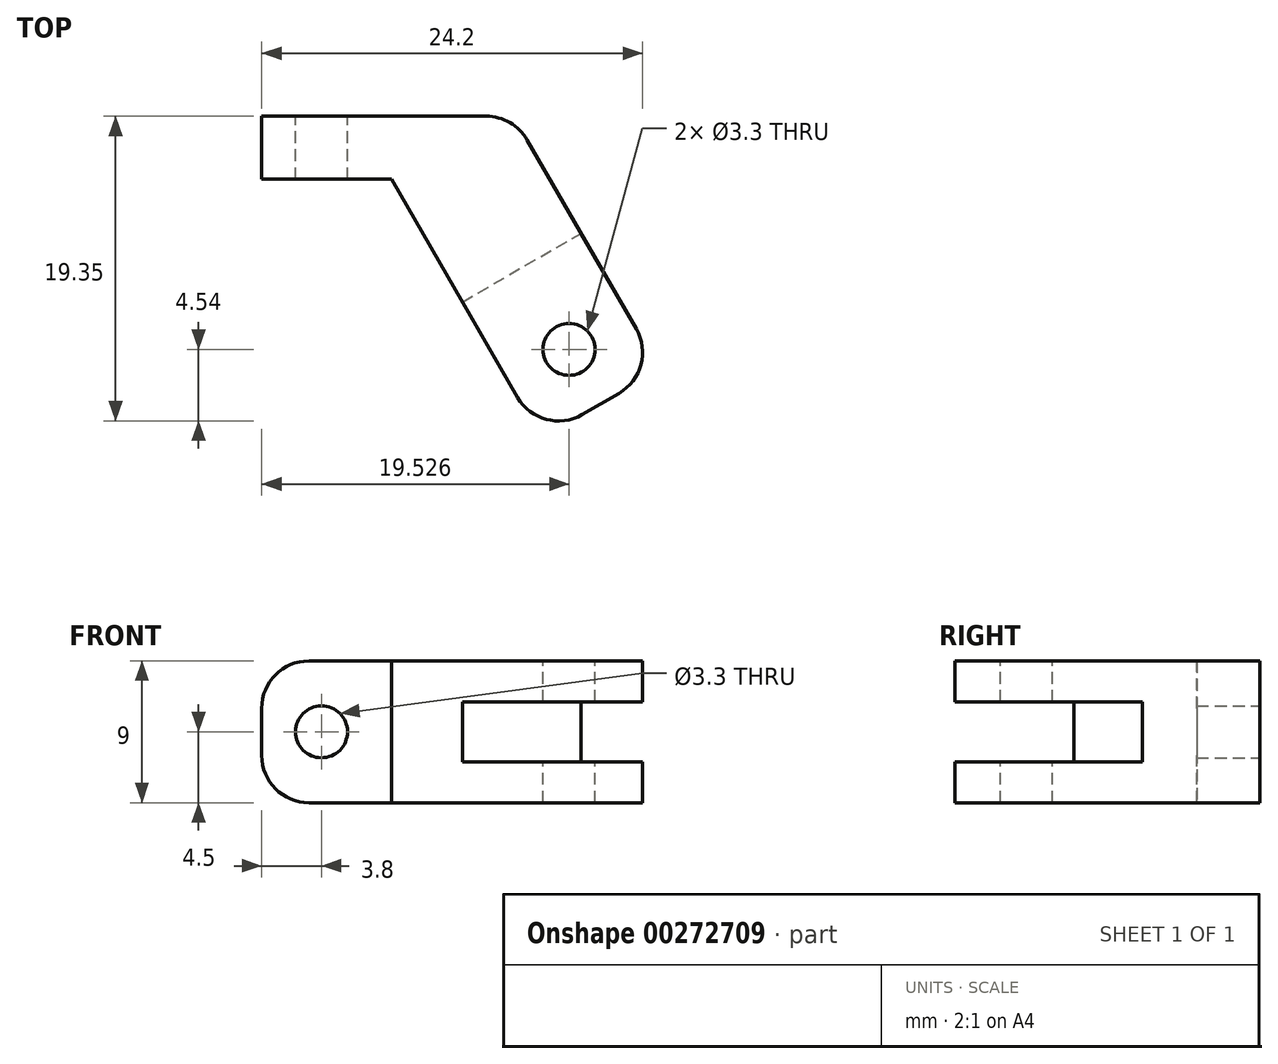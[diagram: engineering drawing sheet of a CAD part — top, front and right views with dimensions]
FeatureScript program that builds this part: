
annotation { "Feature Type Name" : "Feature", "Feature Type Description" : "" }
export const myFeature = defineFeature(function(context is Context, id is Id, definition is map)
    precondition{}
    {
        {
            var Q0;
            Q0=qCreatedBy(makeId("Top.planeOp"),FACE);
            var sketch = newSketch(context, id + "F0", { "sketchPlane" : qUnion([Q0])});
            skLineSegment(sketch, "E0.bottom", {"start": v(-8, 2) * mm, "end": v(8, 2) * mm});
            skLineSegment(sketch, "E0.top", {"start": v(-8, -2) * mm, "end": v(0.26, -2) * mm});
            skLineSegment(sketch, "E0.left", {"start": v(-8, 2) * mm, "end": v(-8, -2) * mm});
            skPoint(sketch, "E0.middle", {"position": v(0, 0) * mm});
            skLineSegment(sketch, "E1", {"start": v(8, 2) * mm, "end": v(17.3, -14.1) * mm});
            skLineSegment(sketch, "E2", {"start": v(17.3, -14.1) * mm, "end": v(9.76, -18.45) * mm});
            skLineSegment(sketch, "E3", {"start": v(9.76, -18.45) * mm, "end": v(0.26, -2) * mm});
            skPoint(sketch, "E4.orphan", {"position": v(8, -2) * mm});
            skSolve(sketch);
        }
        {
            var Q0;
            Q0 = qSketchRegion(id + "F0", true);
            extrude(context, id + "F1", {"entities" : qUnion([Q0]), "depth" : 9 * mm});
        }
        {
            var Q0;
            Q0=makeQuery(id+"F1.opExtrude","SWEPT_FACE",FACE,{"disambiguationData":[OSD([sQuery(id+"F0.wireOp",EDGE,"E0.bottom")])]});
            var sketch = newSketch(context, id + "F2", { "sketchPlane" : qUnion([Q0])});
            skLineSegment(sketch, "E5", {"start": v(8, 4.5) * mm, "end": v(-8, 4.5) * mm, "construction": true});
            skPoint(sketch, "E6", {"position": v(4.2, 4.5) * mm});
            skSolve(sketch);
        }
        {
            var Q0;
            Q0=makeQuery(id+"F1.opExtrude","SWEPT_FACE",FACE,{"disambiguationData":[OSD([sQuery(id+"F0.wireOp",EDGE,"E1")])]});
            var sketch = newSketch(context, id + "F3", { "sketchPlane" : qUnion([Q0])});
            skLineSegment(sketch, "E7", {"start": v(-20.86, 4.5) * mm, "end": v(-2.27, 4.5) * mm, "construction": true});
            skLineSegment(sketch, "E8.bottom", {"start": v(-10.86, 2.6) * mm, "end": v(-30.86, 2.6) * mm});
            skLineSegment(sketch, "E8.top", {"start": v(-10.86, 6.4) * mm, "end": v(-30.86, 6.4) * mm});
            skLineSegment(sketch, "E8.left", {"start": v(-10.86, 2.6) * mm, "end": v(-10.86, 6.4) * mm});
            skLineSegment(sketch, "E8.right", {"start": v(-30.86, 2.6) * mm, "end": v(-30.86, 6.4) * mm});
            skPoint(sketch, "E8.middle", {"position": v(-20.86, 4.5) * mm});
            skSolve(sketch);
        }
        {
            var Q0;
            Q0 = qSketchRegion(id + "F3", true);
            extrude(context, id + "F4", {"entities" : qUnion([Q0]), "operationType" : NewBodyOperationType.REMOVE, "oppositeDirection" : true, "depth" : 25 * mm});
        }
        {
            var Q0;
            Q0=makeQuery(id+"F1.opExtrude","CAP_FACE",FACE,{"disambiguationData":[OSD([sQuery(id+"F0.wireOp",EDGE,"E0.bottom"),sQuery(id+"F0.wireOp",EDGE,"E0.top"),sQuery(id+"F0.wireOp",EDGE,"E0.left"),sQuery(id+"F0.wireOp",EDGE,"E1"),sQuery(id+"F0.wireOp",EDGE,"E2"),sQuery(id+"F0.wireOp",EDGE,"E3")])],"isStart":false});
            var sketch = newSketch(context, id + "F5", { "sketchPlane" : qUnion([Q0])});
            skLineSegment(sketch, "E9", {"start": v(13.53, -16.27) * mm, "end": v(2.97, 2) * mm, "construction": true});
            skPoint(sketch, "E10", {"position": v(11.53, -12.81) * mm});
            skSolve(sketch);
        }
        {
            var Q0;
            Q0=sQuery(id+"F5.wireOp",VERTEX,"E10");
            var Q1;
            Q1=makeQuery(id+"F1.opExtrude","SWEPT_BODY",BODY,{"disambiguationData":[OSD([sQuery(id+"F0.wireOp",EDGE,"E0.bottom"),sQuery(id+"F0.wireOp",EDGE,"E0.top"),sQuery(id+"F0.wireOp",EDGE,"E0.left"),sQuery(id+"F0.wireOp",EDGE,"E1"),sQuery(id+"F0.wireOp",EDGE,"E2"),sQuery(id+"F0.wireOp",EDGE,"E3")])]});
            hole(context, id + "F6", {"style" : HoleStyle.SIMPLE, "endStyle" : HoleEndStyle.THROUGH, "holeDiameter" : 3.3 * mm, "tappedDepth" : 12 * mm, "tapClearance" : 3, "locations" : qUnion([Q0]), "scope" : qUnion([Q1])});
        }
        {
            var Q0;
            Q0=sQuery(id+"F2.wireOp",VERTEX,"E6");
            var Q1;
            Q1=makeQuery(id+"F1.opExtrude","SWEPT_BODY",BODY,{"disambiguationData":[OSD([sQuery(id+"F0.wireOp",EDGE,"E0.bottom"),sQuery(id+"F0.wireOp",EDGE,"E0.top"),sQuery(id+"F0.wireOp",EDGE,"E0.left"),sQuery(id+"F0.wireOp",EDGE,"E1"),sQuery(id+"F0.wireOp",EDGE,"E2"),sQuery(id+"F0.wireOp",EDGE,"E3")])]});
            hole(context, id + "F7", {"style" : HoleStyle.SIMPLE, "endStyle" : HoleEndStyle.THROUGH, "holeDiameter" : 3.3 * mm, "tappedDepth" : 12 * mm, "tapClearance" : 3, "locations" : qUnion([Q0]), "scope" : qUnion([Q1])});
        }
        {
            var Q0;
            Q0=makeQuery(id+"F1.opExtrude","CAP_EDGE",EDGE,{"disambiguationData":[OSD([sQuery(id+"F0.wireOp",EDGE,"E0.left")])],"isStart":false});
            var Q1;
            Q1=makeQuery(id+"F1.opExtrude","CAP_EDGE",EDGE,{"disambiguationData":[OSD([sQuery(id+"F0.wireOp",EDGE,"E0.left")])],"isStart":true});
            var Q2;
            Q2=makeQuery(id+"F1.opExtrude","SWEPT_EDGE",EDGE,{"disambiguationData":[OSD([sQuery(id+"F0.wireOp",EDGE,"E0.bottom"),sQuery(id+"F0.wireOp",EDGE,"E1")])]});
            var Q3;
            {var subQ0=sQuery(id+"F0.wireOp",EDGE,"E2");var subQ1=sQuery(id+"F0.wireOp",EDGE,"E1");Q3=makeQuery(id+"F4.boolean.opBoolean","SPLIT",EDGE,{"disambiguationData":[TD([makeQuery(id+"F4.opExtrude","SWEPT_FACE",FACE,{"disambiguationData":[OSD([sQuery(id+"F3.wireOp",EDGE,"E8.top")])]})])],"derivedFrom":makeQuery(id+"F1.opExtrude","SWEPT_EDGE",EDGE,{"disambiguationData":[OSD([subQ1,subQ0])]})});}
            var Q4;
            {var subQ0=sQuery(id+"F0.wireOp",EDGE,"E2");var subQ1=sQuery(id+"F0.wireOp",EDGE,"E1");Q4=makeQuery(id+"F4.boolean.opBoolean","SPLIT",EDGE,{"disambiguationData":[TD([makeQuery(id+"F4.opExtrude","SWEPT_FACE",FACE,{"disambiguationData":[OSD([sQuery(id+"F3.wireOp",EDGE,"E8.bottom")])]})])],"derivedFrom":makeQuery(id+"F1.opExtrude","SWEPT_EDGE",EDGE,{"disambiguationData":[OSD([subQ1,subQ0])]})});}
            var Q5;
            {var subQ0=sQuery(id+"F0.wireOp",EDGE,"E3");var subQ1=sQuery(id+"F0.wireOp",EDGE,"E2");Q5=makeQuery(id+"F4.boolean.opBoolean","SPLIT",EDGE,{"disambiguationData":[TD([makeQuery(id+"F4.opExtrude","SWEPT_FACE",FACE,{"disambiguationData":[OSD([sQuery(id+"F3.wireOp",EDGE,"E8.bottom")])]})])],"derivedFrom":makeQuery(id+"F1.opExtrude","SWEPT_EDGE",EDGE,{"disambiguationData":[OSD([subQ1,subQ0])]})});}
            var Q6;
            {var subQ0=sQuery(id+"F0.wireOp",EDGE,"E3");var subQ1=sQuery(id+"F0.wireOp",EDGE,"E2");Q6=makeQuery(id+"F4.boolean.opBoolean","SPLIT",EDGE,{"disambiguationData":[TD([makeQuery(id+"F4.opExtrude","SWEPT_FACE",FACE,{"disambiguationData":[OSD([sQuery(id+"F3.wireOp",EDGE,"E8.top")])]})])],"derivedFrom":makeQuery(id+"F1.opExtrude","SWEPT_EDGE",EDGE,{"disambiguationData":[OSD([subQ1,subQ0])]})});}
            fillet(context, id + "F8", {"entities" : qUnion([Q0, Q1, Q2, Q3, Q4, Q5, Q6]), "radius" : 3 * mm, "tangentPropagation" : true, "allowEdgeOverflow" : false});
        }
    });
